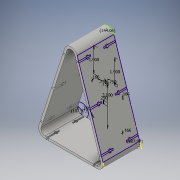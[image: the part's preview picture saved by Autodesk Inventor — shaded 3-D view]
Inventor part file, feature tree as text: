
AUTODESK INVENTOR PART (.ipt)
format: ipt  version: 2016 (Build 200138000, 138)  size: 488,960 bytes
history: native  units: in
note: dims shown in document units (in); Inventor stores cm internally (conversion verified against a paired STEP export)
features: sketch x4, extrude x3, plane x1, mirror x1
ambient origin geometry x8: Origin, YZ Plane, XZ Plane, XY Plane, X Axis, Y Axis, Z Axis, Center Point
bodies: Solid1 (feature_tree)
feature tree (9):
  extrude  "Extrusion1"  Depth=0.5in
  sketch  "Sketch2"  dims[d24=0.18in d25=0.64in]
  extrude  "Extrusion2"  Depth=0.18in
  plane  "Work Plane1"
  mirror  "Mirror1"
  sketch  "Sketch5"  dims[d26=0.64in d27=2.84in d28=0.0in]
  extrude  "Extrusion3"  Depth=2.84in TaperAngle=0.0deg
  sketch  "Sketch1"  dims[d1=0.5in d2=0.5in d3=0.5in d4=4.0in d6=0.495in d10=6.4829in d11=6.4829in d23=0.64in]
  sketch  "Sketch6"  dims[d41=0.25in d42=3.0in d43=0.166in d44=0.166in d45=0.166in d46=0.166in d47=0.15in d48=0.75in d49=0.75in d50=1.9in d51=1.9in d52=0.35in d53=0.35in d54=0.9in d55=0.1in d56=0.9in d57=0.1in d60=0.1in d61=0.9in d62=2.7414in d63=0.112in d64=0.112in d65=0.112in d66=0.112in d67=0.112in d68=0.112in d69=1.0in d70=0.0in d71=2.5in d72=0.35in d73=2.7414in d74=0.9899in d75=0.7419in d76=0.7419in d78=0.607in d79=0.062in d80=0.1in d81=0.192in d82=0.1in d83=0.062in d86=0.607in d87=90.0deg d88=0.062in d89=0.062in d90=0.607in d91=0.15in d92=0.707in d93=0.707in d94=0.607in d96=0.707in d97=0.224in d98=0.15in d99=0.15in d100=0.899in d101=0.607in d102=0.607in d103=0.192in d104=0.192in d105=0.1in d106=0.062in d107=0.062in d108=0.1in d109=0.1in d110=0.062in d111=0.062in d112=0.1in d113=0.224in d114=0.607in d115=0.707in d116=3.5in d117=3.376in d118=0.1in d119=0.607in d120=0.607in d121=0.1in d122=0.1in d123=0.1in d124=0.192in d125=0.192in d126=0.062in d127=0.062in d128=0.224in d129=0.1in d130=1.0in d131=0.0in]
